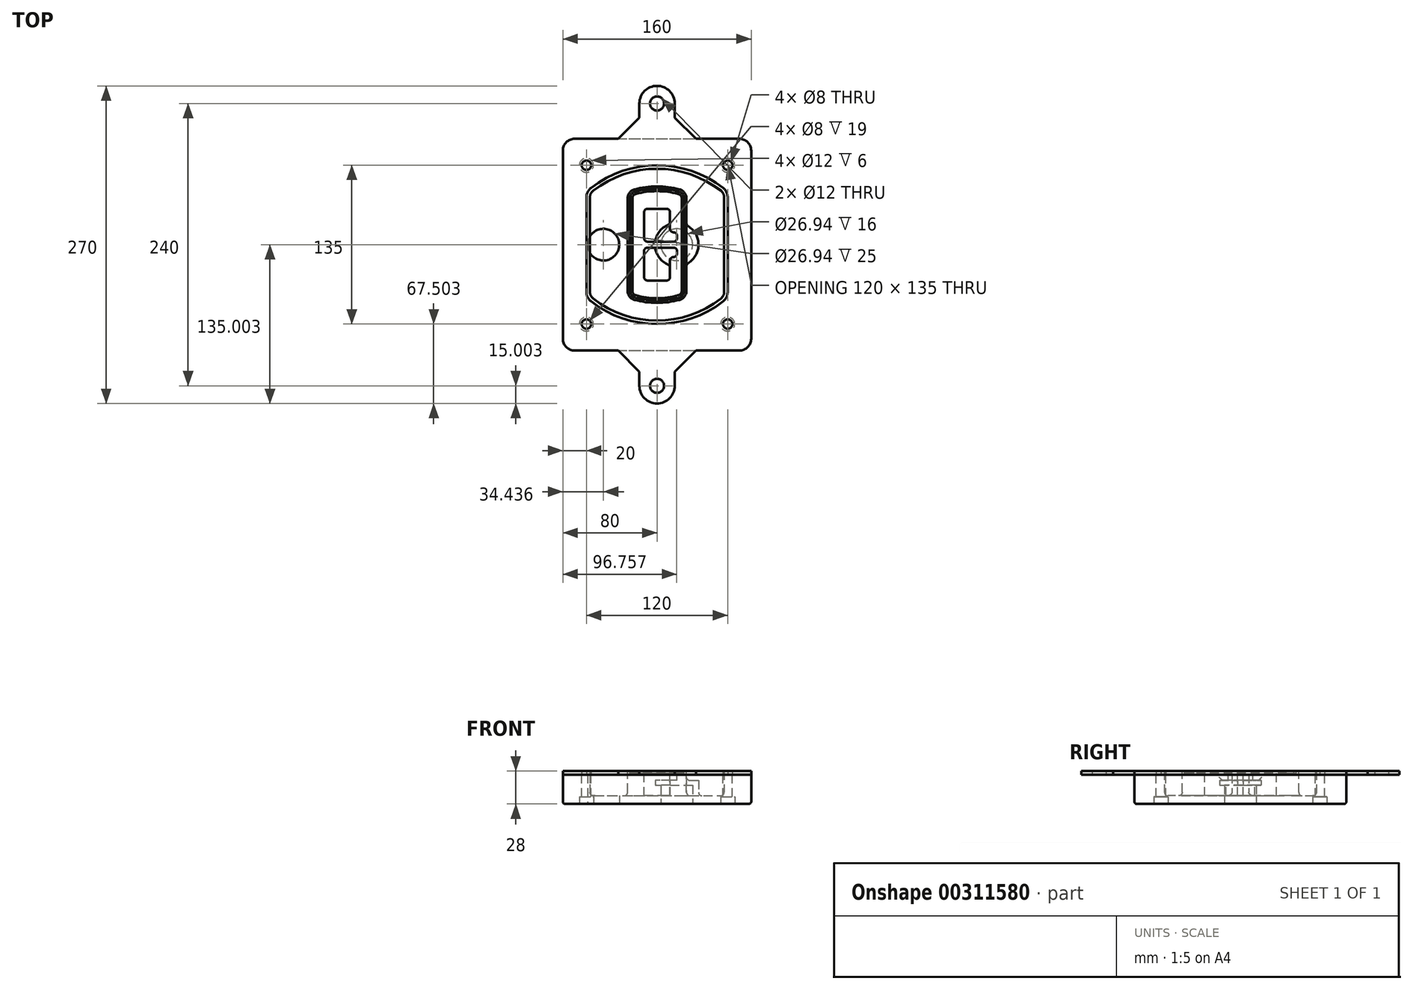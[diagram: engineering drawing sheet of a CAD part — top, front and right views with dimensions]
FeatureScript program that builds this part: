
annotation { "Feature Type Name" : "Feature", "Feature Type Description" : "" }
export const myFeature = defineFeature(function(context is Context, id is Id, definition is map)
    precondition{}
    {
        {
            var Q0;
            Q0=qCreatedBy(makeId("Top.planeOp"),FACE);
            var sketch = newSketch(context, id + "F0", { "sketchPlane" : qUnion([Q0])});
            skPoint(sketch, "E0.rect.middle", {"position": v(0, 0) * mm});
            skLineSegment(sketch, "E1.bottom", {"start": v(24.05, 28.38) * mm, "end": v(164.05, 28.38) * mm});
            skLineSegment(sketch, "E1.top", {"start": v(24.05, 208.38) * mm, "end": v(164.05, 208.38) * mm});
            skLineSegment(sketch, "E1.left", {"start": v(14.05, 38.38) * mm, "end": v(14.05, 198.38) * mm});
            skLineSegment(sketch, "E1.right", {"start": v(174.05, 38.38) * mm, "end": v(174.05, 198.38) * mm});
            skLineSegment(sketch, "E2", {"start": v(14.05, 208.38) * mm, "end": v(174.05, 28.38) * mm, "construction": true});
            skLineSegment(sketch, "E3", {"start": v(174.05, 208.38) * mm, "end": v(14.05, 28.38) * mm, "construction": true});
            skCircle(sketch, "E4", {"center": v(34.05, 185.88) * mm, "radius": 4 * mm});
            skCircle(sketch, "E5", {"center": v(154.05, 185.88) * mm, "radius": 4 * mm});
            skCircle(sketch, "E6", {"center": v(154.05, 50.88) * mm, "radius": 4 * mm});
            skCircle(sketch, "E7", {"center": v(34.05, 50.88) * mm, "radius": 4 * mm});
            skLineSegment(sketch, "E8", {"start": v(34.05, 185.88) * mm, "end": v(154.05, 185.88) * mm, "construction": true});
            skLineSegment(sketch, "E9", {"start": v(154.05, 185.88) * mm, "end": v(154.05, 50.88) * mm, "construction": true});
            skLineSegment(sketch, "E10", {"start": v(154.05, 50.88) * mm, "end": v(34.05, 50.88) * mm, "construction": true});
            skLineSegment(sketch, "E11", {"start": v(34.05, 50.88) * mm, "end": v(34.05, 185.88) * mm, "construction": true});
            skLineSegment(sketch, "E12", {"start": v(34.05, 158.68) * mm, "end": v(34.05, 78.09) * mm});
            skLineSegment(sketch, "E13", {"start": v(154.05, 158.68) * mm, "end": v(154.05, 78.09) * mm});
            skArc(sketch, "E14", {"start": v(150.2, 166.56) * mm, "mid": v(94.05, 185.88) * mm, "end": v(37.9, 166.56) * mm});
            skArc(sketch, "E15", {"start": v(37.9, 70.2) * mm, "mid": v(94.05, 50.88) * mm, "end": v(150.2, 70.2) * mm});
            skLineSegment(sketch, "E16", {"start": v(34.05, 118.38) * mm, "end": v(154.05, 118.38) * mm, "construction": true});
            skPoint(sketch, "E17.visualSharp", {"position": v(34.05, 73.38) * mm});
            skArc(sketch, "E17.filletArc", {"start": v(34.05, 78.09) * mm, "mid": v(35.06, 73.7) * mm, "end": v(37.9, 70.2) * mm});
            skPoint(sketch, "E18.visualSharp", {"position": v(34.05, 163.38) * mm});
            skArc(sketch, "E18.filletArc", {"start": v(37.9, 166.56) * mm, "mid": v(35.06, 163.06) * mm, "end": v(34.05, 158.68) * mm});
            skPoint(sketch, "E19.visualSharp", {"position": v(154.05, 163.38) * mm});
            skArc(sketch, "E19.filletArc", {"start": v(154.05, 158.68) * mm, "mid": v(153.04, 163.06) * mm, "end": v(150.2, 166.56) * mm});
            skPoint(sketch, "E20.visualSharp", {"position": v(154.05, 73.38) * mm});
            skArc(sketch, "E20.filletArc", {"start": v(150.2, 70.2) * mm, "mid": v(153.04, 73.7) * mm, "end": v(154.05, 78.09) * mm});
            skPoint(sketch, "E21.visualSharp", {"position": v(14.05, 208.38) * mm});
            skArc(sketch, "E21.filletArc", {"start": v(24.05, 208.38) * mm, "mid": v(16.98, 205.45) * mm, "end": v(14.05, 198.38) * mm});
            skPoint(sketch, "E22.visualSharp", {"position": v(174.05, 208.38) * mm});
            skArc(sketch, "E22.filletArc", {"start": v(174.05, 198.38) * mm, "mid": v(171.12, 205.45) * mm, "end": v(164.05, 208.38) * mm});
            skPoint(sketch, "E23.visualSharp", {"position": v(174.05, 28.38) * mm});
            skArc(sketch, "E23.filletArc", {"start": v(164.05, 28.38) * mm, "mid": v(171.12, 31.31) * mm, "end": v(174.05, 38.38) * mm});
            skPoint(sketch, "E24.visualSharp", {"position": v(14.05, 28.38) * mm});
            skArc(sketch, "E24.filletArc", {"start": v(14.05, 38.38) * mm, "mid": v(16.98, 31.31) * mm, "end": v(24.05, 28.38) * mm});
            skArc(sketch, "E25.0", {"start": v(151.05, 158.68) * mm, "mid": v(150.34, 161.75) * mm, "end": v(148.36, 164.2) * mm});
            skLineSegment(sketch, "E25.1", {"start": v(151.05, 158.68) * mm, "end": v(151.05, 78.09) * mm});
            skArc(sketch, "E25.2", {"start": v(148.36, 72.57) * mm, "mid": v(150.34, 75.02) * mm, "end": v(151.05, 78.09) * mm});
            skArc(sketch, "E25.3", {"start": v(39.74, 72.57) * mm, "mid": v(94.05, 53.88) * mm, "end": v(148.36, 72.57) * mm});
            skArc(sketch, "E25.4", {"start": v(37.05, 78.09) * mm, "mid": v(37.76, 75.02) * mm, "end": v(39.74, 72.57) * mm});
            skArc(sketch, "E25.5", {"start": v(148.36, 164.2) * mm, "mid": v(94.05, 182.88) * mm, "end": v(39.74, 164.2) * mm});
            skLineSegment(sketch, "E25.6", {"start": v(37.05, 158.68) * mm, "end": v(37.05, 78.09) * mm});
            skArc(sketch, "E25.7", {"start": v(39.74, 164.2) * mm, "mid": v(37.76, 161.75) * mm, "end": v(37.05, 158.68) * mm});
            skArc(sketch, "E26.0", {"start": v(35.43, 169.71) * mm, "mid": v(31.47, 164.82) * mm, "end": v(30.05, 158.68) * mm});
            skArc(sketch, "E26.1", {"start": v(152.67, 169.71) * mm, "mid": v(94.05, 189.88) * mm, "end": v(35.43, 169.71) * mm});
            skArc(sketch, "E26.2", {"start": v(158.05, 158.68) * mm, "mid": v(156.63, 164.82) * mm, "end": v(152.67, 169.71) * mm});
            skLineSegment(sketch, "E26.3", {"start": v(158.05, 158.68) * mm, "end": v(158.05, 78.09) * mm});
            skArc(sketch, "E26.4", {"start": v(152.67, 67.05) * mm, "mid": v(156.63, 71.95) * mm, "end": v(158.05, 78.09) * mm});
            skLineSegment(sketch, "E26.5", {"start": v(30.05, 158.68) * mm, "end": v(30.05, 78.09) * mm});
            skArc(sketch, "E26.6", {"start": v(35.43, 67.05) * mm, "mid": v(94.05, 46.88) * mm, "end": v(152.67, 67.05) * mm});
            skArc(sketch, "E26.7", {"start": v(30.05, 78.09) * mm, "mid": v(31.47, 71.95) * mm, "end": v(35.43, 67.05) * mm});
            skSolve(sketch);
        }
        {
            var Q0;
            Q0=makeQuery(id+"F0.imprint","IMPRINT",FACE,{"disambiguationData":[TD([[makeQuery(id+"F0.imprint","IMPRINT",EDGE,{"derivedFrom":sQuery(id+"F0.wireOp",EDGE,"E1.bottom")}),1.0]])]});
            var Q1;
            Q1=makeQuery(id+"F0.imprint","IMPRINT",FACE,{"disambiguationData":[TD([[makeQuery(id+"F0.imprint","IMPRINT",EDGE,{"derivedFrom":sQuery(id+"F0.wireOp",EDGE,"E12")}),1.0]])]});
            var Q2;
            Q2=makeQuery(id+"F0.imprint","IMPRINT",FACE,{"disambiguationData":[TD([[makeQuery(id+"F0.imprint","IMPRINT",EDGE,{"derivedFrom":sQuery(id+"F0.wireOp",EDGE,"E25.0")}),1.0]])]});
            var Q3;
            Q3=makeQuery(id+"F0.imprint","IMPRINT",FACE,{"disambiguationData":[TD([[makeQuery(id+"F0.imprint","IMPRINT",EDGE,{"derivedFrom":sQuery(id+"F0.wireOp",EDGE,"E12")}),-1.0]])]});
            extrude(context, id + "F1", {"entities" : qUnion([Q0, Q1, Q2, Q3]), "oppositeDirection" : true, "depth" : 25 * mm});
        }
        {
            var Q0;
            Q0=makeQuery(id+"F0.imprint","IMPRINT",FACE,{"disambiguationData":[TD([[makeQuery(id+"F0.imprint","IMPRINT",EDGE,{"derivedFrom":sQuery(id+"F0.wireOp",EDGE,"E12")}),1.0]])]});
            extrude(context, id + "F2", {"entities" : qUnion([Q0]), "operationType" : NewBodyOperationType.ADD, "depth" : 3 * mm});
        }
        {
            var Q0;
            Q0=makeQuery(id+"F0.imprint","IMPRINT",FACE,{"disambiguationData":[TD([[makeQuery(id+"F0.imprint","IMPRINT",EDGE,{"derivedFrom":sQuery(id+"F0.wireOp",EDGE,"E25.0")}),1.0]])]});
            extrude(context, id + "F3", {"entities" : qUnion([Q0]), "operationType" : NewBodyOperationType.REMOVE, "oppositeDirection" : true, "depth" : 18 * mm});
        }
        {
            var Q0;
            Q0=makeQuery(id+"F2.opExtrude","CAP_FACE",FACE,{"disambiguationData":[OSD([sQuery(id+"F0.wireOp",EDGE,"E12"),sQuery(id+"F0.wireOp",EDGE,"E13"),sQuery(id+"F0.wireOp",EDGE,"E14"),sQuery(id+"F0.wireOp",EDGE,"E15"),sQuery(id+"F0.wireOp",EDGE,"E17.filletArc"),sQuery(id+"F0.wireOp",EDGE,"E18.filletArc"),sQuery(id+"F0.wireOp",EDGE,"E19.filletArc"),sQuery(id+"F0.wireOp",EDGE,"E20.filletArc"),sQuery(id+"F0.wireOp",EDGE,"E25.0"),sQuery(id+"F0.wireOp",EDGE,"E25.1"),sQuery(id+"F0.wireOp",EDGE,"E25.2"),sQuery(id+"F0.wireOp",EDGE,"E25.3"),sQuery(id+"F0.wireOp",EDGE,"E25.4"),sQuery(id+"F0.wireOp",EDGE,"E25.5"),sQuery(id+"F0.wireOp",EDGE,"E25.6"),sQuery(id+"F0.wireOp",EDGE,"E25.7")])],"isStart":false});
            var sketch = newSketch(context, id + "F4", { "sketchPlane" : qUnion([Q0])});
            skArc(sketch, "E27.0", {"start": v(74.97, 71.41) * mm, "mid": v(94.05, 68.88) * mm, "end": v(113.13, 71.41) * mm});
            skArc(sketch, "E28.0", {"start": v(113.13, 165.35) * mm, "mid": v(94.05, 167.88) * mm, "end": v(74.97, 165.35) * mm});
            skLineSegment(sketch, "E29", {"start": v(69.05, 157.63) * mm, "end": v(69.05, 79.14) * mm});
            skLineSegment(sketch, "E30", {"start": v(119.05, 157.63) * mm, "end": v(119.05, 79.14) * mm});
            skLineSegment(sketch, "E31", {"start": v(69.05, 163.48) * mm, "end": v(119.05, 163.48) * mm, "construction": true});
            skLineSegment(sketch, "E32", {"start": v(69.05, 73.28) * mm, "end": v(119.05, 73.28) * mm, "construction": true});
            skPoint(sketch, "E33.visualSharp", {"position": v(69.05, 163.48) * mm});
            skArc(sketch, "E33.filletArc", {"start": v(74.97, 165.35) * mm, "mid": v(70.7, 162.5) * mm, "end": v(69.05, 157.63) * mm});
            skPoint(sketch, "E34.visualSharp", {"position": v(119.05, 163.48) * mm});
            skArc(sketch, "E34.filletArc", {"start": v(119.05, 157.63) * mm, "mid": v(117.4, 162.5) * mm, "end": v(113.13, 165.35) * mm});
            skPoint(sketch, "E35.visualSharp", {"position": v(119.05, 73.28) * mm});
            skArc(sketch, "E35.filletArc", {"start": v(113.13, 71.41) * mm, "mid": v(117.4, 74.27) * mm, "end": v(119.05, 79.14) * mm});
            skPoint(sketch, "E36.visualSharp", {"position": v(69.05, 73.28) * mm});
            skArc(sketch, "E36.filletArc", {"start": v(69.05, 79.14) * mm, "mid": v(70.7, 74.27) * mm, "end": v(74.97, 71.41) * mm});
            skArc(sketch, "E37.0", {"start": v(148.36, 164.2) * mm, "mid": v(94.05, 182.88) * mm, "end": v(39.74, 164.2) * mm});
            skArc(sketch, "E37.1", {"start": v(39.74, 164.2) * mm, "mid": v(37.76, 161.75) * mm, "end": v(37.05, 158.68) * mm});
            skLineSegment(sketch, "E37.2", {"start": v(37.05, 158.68) * mm, "end": v(37.05, 78.09) * mm});
            skArc(sketch, "E37.3", {"start": v(37.05, 78.09) * mm, "mid": v(37.76, 75.02) * mm, "end": v(39.74, 72.57) * mm});
            skArc(sketch, "E37.4", {"start": v(39.74, 72.57) * mm, "mid": v(94.05, 53.88) * mm, "end": v(148.36, 72.57) * mm});
            skArc(sketch, "E37.5", {"start": v(148.36, 72.57) * mm, "mid": v(150.34, 75.02) * mm, "end": v(151.05, 78.09) * mm});
            skLineSegment(sketch, "E37.6", {"start": v(151.05, 158.68) * mm, "end": v(151.05, 78.09) * mm});
            skArc(sketch, "E37.7", {"start": v(151.05, 158.68) * mm, "mid": v(150.34, 161.75) * mm, "end": v(148.36, 164.2) * mm});
            skLineSegment(sketch, "E38.0", {"start": v(117.05, 157.63) * mm, "end": v(117.05, 79.14) * mm});
            skArc(sketch, "E38.1", {"start": v(112.61, 73.34) * mm, "mid": v(115.81, 75.49) * mm, "end": v(117.05, 79.14) * mm});
            skArc(sketch, "E38.2", {"start": v(75.49, 73.34) * mm, "mid": v(94.05, 70.88) * mm, "end": v(112.61, 73.34) * mm});
            skArc(sketch, "E38.3", {"start": v(71.05, 79.14) * mm, "mid": v(72.29, 75.49) * mm, "end": v(75.49, 73.34) * mm});
            skLineSegment(sketch, "E38.4", {"start": v(71.05, 157.63) * mm, "end": v(71.05, 79.14) * mm});
            skArc(sketch, "E38.5", {"start": v(117.05, 157.63) * mm, "mid": v(115.81, 161.28) * mm, "end": v(112.61, 163.42) * mm});
            skArc(sketch, "E38.6", {"start": v(75.49, 163.42) * mm, "mid": v(72.29, 161.28) * mm, "end": v(71.05, 157.63) * mm});
            skArc(sketch, "E38.7", {"start": v(112.61, 163.42) * mm, "mid": v(94.05, 165.88) * mm, "end": v(75.49, 163.42) * mm});
            skArc(sketch, "E39.0", {"start": v(115.05, 157.63) * mm, "mid": v(114.23, 160.06) * mm, "end": v(112.1, 161.5) * mm});
            skLineSegment(sketch, "E39.1", {"start": v(115.05, 157.63) * mm, "end": v(115.05, 79.14) * mm});
            skArc(sketch, "E39.2", {"start": v(112.1, 75.27) * mm, "mid": v(114.23, 76.7) * mm, "end": v(115.05, 79.14) * mm});
            skArc(sketch, "E39.3", {"start": v(76, 75.27) * mm, "mid": v(94.05, 72.88) * mm, "end": v(112.1, 75.27) * mm});
            skArc(sketch, "E39.4", {"start": v(73.05, 79.14) * mm, "mid": v(73.87, 76.7) * mm, "end": v(76, 75.27) * mm});
            skArc(sketch, "E39.5", {"start": v(112.1, 161.5) * mm, "mid": v(94.05, 163.88) * mm, "end": v(76, 161.5) * mm});
            skLineSegment(sketch, "E39.6", {"start": v(73.05, 157.63) * mm, "end": v(73.05, 79.14) * mm});
            skArc(sketch, "E39.7", {"start": v(76, 161.5) * mm, "mid": v(73.87, 160.06) * mm, "end": v(73.05, 157.63) * mm});
            skLineSegment(sketch, "E40", {"start": v(69.05, 118.38) * mm, "end": v(119.05, 118.38) * mm, "construction": true});
            skLineSegment(sketch, "E41", {"start": v(83.05, 123.88) * mm, "end": v(83.05, 145.88) * mm});
            skLineSegment(sketch, "E42", {"start": v(86.05, 148.88) * mm, "end": v(102.05, 148.88) * mm});
            skLineSegment(sketch, "E43", {"start": v(105.05, 145.88) * mm, "end": v(105.05, 131.88) * mm});
            skLineSegment(sketch, "E44", {"start": v(108.05, 128.88) * mm, "end": v(108.05, 128.88) * mm});
            skLineSegment(sketch, "E45", {"start": v(111.05, 125.88) * mm, "end": v(111.05, 123.88) * mm});
            skLineSegment(sketch, "E46", {"start": v(108.05, 120.88) * mm, "end": v(86.05, 120.88) * mm});
            skPoint(sketch, "E47.visualSharp", {"position": v(83.05, 148.88) * mm});
            skArc(sketch, "E47.filletArc", {"start": v(86.05, 148.88) * mm, "mid": v(83.93, 148) * mm, "end": v(83.05, 145.88) * mm});
            skPoint(sketch, "E48.visualSharp", {"position": v(105.05, 148.88) * mm});
            skArc(sketch, "E48.filletArc", {"start": v(105.05, 145.88) * mm, "mid": v(104.17, 148) * mm, "end": v(102.05, 148.88) * mm});
            skPoint(sketch, "E49.visualSharp", {"position": v(105.05, 128.88) * mm});
            skArc(sketch, "E49.filletArc", {"start": v(105.05, 131.88) * mm, "mid": v(105.93, 129.76) * mm, "end": v(108.05, 128.88) * mm});
            skPoint(sketch, "E50.visualSharp", {"position": v(111.05, 128.88) * mm});
            skArc(sketch, "E50.filletArc", {"start": v(111.05, 125.88) * mm, "mid": v(110.17, 128) * mm, "end": v(108.05, 128.88) * mm});
            skPoint(sketch, "E51.visualSharp", {"position": v(111.05, 120.88) * mm});
            skArc(sketch, "E51.filletArc", {"start": v(108.05, 120.88) * mm, "mid": v(110.17, 121.76) * mm, "end": v(111.05, 123.88) * mm});
            skPoint(sketch, "E52.visualSharp", {"position": v(83.05, 120.88) * mm});
            skArc(sketch, "E52.filletArc", {"start": v(83.05, 123.88) * mm, "mid": v(83.93, 121.76) * mm, "end": v(86.05, 120.88) * mm});
            skLineSegment(sketch, "E53.0.MirrorCS", {"start": v(108.05, 115.88) * mm, "end": v(86.05, 115.88) * mm});
            skArc(sketch, "E54.0.MirrorCS", {"start": v(83.05, 112.88) * mm, "mid": v(83.93, 115) * mm, "end": v(86.05, 115.88) * mm});
            skLineSegment(sketch, "E55.0.MirrorCS", {"start": v(83.05, 112.88) * mm, "end": v(83.05, 90.88) * mm});
            skArc(sketch, "E56.0.MirrorCS", {"start": v(86.05, 87.88) * mm, "mid": v(83.93, 88.76) * mm, "end": v(83.05, 90.88) * mm});
            skLineSegment(sketch, "E57.0.MirrorCS", {"start": v(86.05, 87.88) * mm, "end": v(102.05, 87.88) * mm});
            skArc(sketch, "E58.0.MirrorCS", {"start": v(105.05, 90.88) * mm, "mid": v(104.17, 88.76) * mm, "end": v(102.05, 87.88) * mm});
            skLineSegment(sketch, "E59.0.MirrorCS", {"start": v(105.05, 90.88) * mm, "end": v(105.05, 104.88) * mm});
            skArc(sketch, "E60.0.MirrorCS", {"start": v(105.05, 104.88) * mm, "mid": v(105.93, 107) * mm, "end": v(108.05, 107.88) * mm});
            skArc(sketch, "E61.0.MirrorCS", {"start": v(111.05, 110.88) * mm, "mid": v(110.17, 108.76) * mm, "end": v(108.05, 107.88) * mm});
            skLineSegment(sketch, "E62.0.MirrorCS", {"start": v(111.05, 110.88) * mm, "end": v(111.05, 112.88) * mm});
            skArc(sketch, "E63.0.MirrorCS", {"start": v(108.05, 115.88) * mm, "mid": v(110.17, 115) * mm, "end": v(111.05, 112.88) * mm});
            skSolve(sketch);
        }
        {
            var Q0;
            Q0=makeQuery(id+"F4.imprint","IMPRINT",FACE,{"disambiguationData":[TD([[makeQuery(id+"F4.imprint","IMPRINT",EDGE,{"derivedFrom":sQuery(id+"F4.wireOp",EDGE,"E27.0")}),1.0]])]});
            var Q1;
            Q1=makeQuery(id+"F4.imprint","IMPRINT",FACE,{"disambiguationData":[TD([[makeQuery(id+"F4.imprint","IMPRINT",EDGE,{"derivedFrom":sQuery(id+"F4.wireOp",EDGE,"E38.0")}),-1.0]])]});
            var Q2;
            Q2=makeQuery(id+"F4.imprint","IMPRINT",FACE,{"disambiguationData":[TD([[makeQuery(id+"F4.imprint","IMPRINT",EDGE,{"derivedFrom":sQuery(id+"F4.wireOp",EDGE,"E39.0")}),1.0]])]});
            extrude(context, id + "F5", {"entities" : qUnion([Q0, Q1, Q2]), "operationType" : NewBodyOperationType.ADD, "endBound" : BoundingType.UP_TO_NEXT, "oppositeDirection" : true, "depth" : 25 * mm});
        }
        {
            var Q0;
            Q0=makeQuery(id+"F4.imprint","IMPRINT",FACE,{"disambiguationData":[TD([[makeQuery(id+"F4.imprint","IMPRINT",EDGE,{"derivedFrom":sQuery(id+"F4.wireOp",EDGE,"E38.0")}),-1.0]])]});
            extrude(context, id + "F6", {"entities" : qUnion([Q0]), "operationType" : NewBodyOperationType.REMOVE, "oppositeDirection" : true, "depth" : 2 * mm});
        }
        {
            var Q0;
            Q0=makeQuery(id+"F1.opExtrude","CAP_FACE",FACE,{"disambiguationData":[OSD([sQuery(id+"F0.wireOp",EDGE,"E1.bottom"),sQuery(id+"F0.wireOp",EDGE,"E1.top"),sQuery(id+"F0.wireOp",EDGE,"E1.left"),sQuery(id+"F0.wireOp",EDGE,"E1.right"),sQuery(id+"F0.wireOp",EDGE,"E4"),sQuery(id+"F0.wireOp",EDGE,"E5"),sQuery(id+"F0.wireOp",EDGE,"E6"),sQuery(id+"F0.wireOp",EDGE,"E7"),sQuery(id+"F0.wireOp",EDGE,"E21.filletArc"),sQuery(id+"F0.wireOp",EDGE,"E22.filletArc"),sQuery(id+"F0.wireOp",EDGE,"E23.filletArc"),sQuery(id+"F0.wireOp",EDGE,"E24.filletArc")])],"isStart":false});
            var sketch = newSketch(context, id + "F7", { "sketchPlane" : qUnion([Q0])});
            skCircle(sketch, "E64", {"center": v(110.8, -118.38) * mm, "radius": 13.47 * mm});
            skCircle(sketch, "E65", {"center": v(48.49, -118.38) * mm, "radius": 13.47 * mm});
            skLineSegment(sketch, "E66", {"start": v(174.05, -118.38) * mm, "end": v(14.05, -118.38) * mm});
            skCircle(sketch, "E67", {"center": v(110.8, -118.38) * mm, "radius": 18.47 * mm});
            skCircle(sketch, "E68", {"center": v(154.05, -185.88) * mm, "radius": 6 * mm});
            skCircle(sketch, "E69", {"center": v(34.05, -185.88) * mm, "radius": 6 * mm});
            skCircle(sketch, "E70", {"center": v(34.05, -50.88) * mm, "radius": 6 * mm});
            skCircle(sketch, "E71", {"center": v(154.05, -50.88) * mm, "radius": 6 * mm});
            skSolve(sketch);
        }
        {
            var Q0;
            {var subQ1=sQuery(id+"F7.wireOp",EDGE,"E66");var subQ4=sQuery(id+"F7.wireOp",EDGE,"E64");var subQ6=makeQuery(id+"F7.imprint","INTERSECT",VERTEX,{"disambiguationData":[OD(0.0)],"derivedFrom":[subQ4,subQ1]});Q0=makeQuery(id+"F7.imprint","IMPRINT",FACE,{"disambiguationData":[TD([[makeQuery(id+"F7.imprint","IMPRINT",EDGE,{"disambiguationData":[TD([[subQ6,-1.0]])],"derivedFrom":subQ4}),-1.0]])]});}
            var Q1;
            {var subQ0=sQuery(id+"F7.wireOp",EDGE,"E66");var subQ1=sQuery(id+"F7.wireOp",EDGE,"E64");var subQ3=makeQuery(id+"F7.imprint","INTERSECT",VERTEX,{"disambiguationData":[OD(0.0)],"derivedFrom":[subQ1,subQ0]});Q1=makeQuery(id+"F7.imprint","IMPRINT",FACE,{"disambiguationData":[TD([[makeQuery(id+"F7.imprint","IMPRINT",EDGE,{"disambiguationData":[TD([[subQ3,-1.0]])],"derivedFrom":subQ1}),1.0]])]});}
            var Q2;
            {var subQ0=sQuery(id+"F7.wireOp",EDGE,"E66");var subQ1=sQuery(id+"F7.wireOp",EDGE,"E64");var subQ3=makeQuery(id+"F7.imprint","INTERSECT",VERTEX,{"disambiguationData":[OD(0.0)],"derivedFrom":[subQ1,subQ0]});Q2=makeQuery(id+"F7.imprint","IMPRINT",FACE,{"disambiguationData":[TD([[makeQuery(id+"F7.imprint","IMPRINT",EDGE,{"disambiguationData":[TD([[subQ3,1.0]])],"derivedFrom":subQ1}),1.0]])]});}
            var Q3;
            {var subQ1=sQuery(id+"F7.wireOp",EDGE,"E66");var subQ4=sQuery(id+"F7.wireOp",EDGE,"E64");var subQ6=makeQuery(id+"F7.imprint","INTERSECT",VERTEX,{"disambiguationData":[OD(0.0)],"derivedFrom":[subQ4,subQ1]});Q3=makeQuery(id+"F7.imprint","IMPRINT",FACE,{"disambiguationData":[TD([[makeQuery(id+"F7.imprint","IMPRINT",EDGE,{"disambiguationData":[TD([[subQ6,1.0]])],"derivedFrom":subQ4}),-1.0]])]});}
            extrude(context, id + "F8", {"entities" : qUnion([Q0, Q1, Q2, Q3]), "operationType" : NewBodyOperationType.ADD, "oppositeDirection" : true, "depth" : 20 * mm});
        }
        {
            var Q0;
            {var subQ0=sQuery(id+"F7.wireOp",EDGE,"E66");var subQ1=sQuery(id+"F7.wireOp",EDGE,"E64");var subQ3=makeQuery(id+"F7.imprint","INTERSECT",VERTEX,{"disambiguationData":[OD(0.0)],"derivedFrom":[subQ1,subQ0]});Q0=makeQuery(id+"F7.imprint","IMPRINT",FACE,{"disambiguationData":[TD([[makeQuery(id+"F7.imprint","IMPRINT",EDGE,{"disambiguationData":[TD([[subQ3,-1.0]])],"derivedFrom":subQ1}),1.0]])]});}
            var Q1;
            {var subQ0=sQuery(id+"F7.wireOp",EDGE,"E66");var subQ1=sQuery(id+"F7.wireOp",EDGE,"E64");var subQ3=makeQuery(id+"F7.imprint","INTERSECT",VERTEX,{"disambiguationData":[OD(0.0)],"derivedFrom":[subQ1,subQ0]});Q1=makeQuery(id+"F7.imprint","IMPRINT",FACE,{"disambiguationData":[TD([[makeQuery(id+"F7.imprint","IMPRINT",EDGE,{"disambiguationData":[TD([[subQ3,1.0]])],"derivedFrom":subQ1}),1.0]])]});}
            extrude(context, id + "F9", {"entities" : qUnion([Q0, Q1]), "operationType" : NewBodyOperationType.REMOVE, "oppositeDirection" : true, "depth" : 16 * mm});
        }
        {
            var Q0;
            {var subQ0=sQuery(id+"F7.wireOp",EDGE,"E66");var subQ1=sQuery(id+"F7.wireOp",EDGE,"E65");var subQ3=makeQuery(id+"F7.imprint","INTERSECT",VERTEX,{"disambiguationData":[OD(0.0)],"derivedFrom":[subQ1,subQ0]});Q0=makeQuery(id+"F7.imprint","IMPRINT",FACE,{"disambiguationData":[TD([[makeQuery(id+"F7.imprint","IMPRINT",EDGE,{"disambiguationData":[TD([[subQ3,-1.0]])],"derivedFrom":subQ1}),1.0]])]});}
            var Q1;
            {var subQ0=sQuery(id+"F7.wireOp",EDGE,"E66");var subQ1=sQuery(id+"F7.wireOp",EDGE,"E65");var subQ3=makeQuery(id+"F7.imprint","INTERSECT",VERTEX,{"disambiguationData":[OD(0.0)],"derivedFrom":[subQ1,subQ0]});Q1=makeQuery(id+"F7.imprint","IMPRINT",FACE,{"disambiguationData":[TD([[makeQuery(id+"F7.imprint","IMPRINT",EDGE,{"disambiguationData":[TD([[subQ3,1.0]])],"derivedFrom":subQ1}),1.0]])]});}
            extrude(context, id + "F10", {"entities" : qUnion([Q0, Q1]), "operationType" : NewBodyOperationType.REMOVE, "oppositeDirection" : true, "depth" : 25 * mm});
        }
        {
            var Q0;
            Q0=makeQuery(id+"F7.imprint","IMPRINT",FACE,{"disambiguationData":[TD([[makeQuery(id+"F7.imprint","IMPRINT",EDGE,{"derivedFrom":sQuery(id+"F7.wireOp",EDGE,"E68")}),1.0]])]});
            var Q1;
            Q1=makeQuery(id+"F7.imprint","IMPRINT",FACE,{"disambiguationData":[TD([[makeQuery(id+"F7.imprint","IMPRINT",EDGE,{"derivedFrom":makeQuery(id+"F1.opExtrude","CAP_EDGE",EDGE,{"disambiguationData":[OSD([sQuery(id+"F0.wireOp",EDGE,"E5")])],"isStart":false})}),-1.0]])]});
            var Q2;
            Q2=makeQuery(id+"F7.imprint","IMPRINT",FACE,{"disambiguationData":[TD([[makeQuery(id+"F7.imprint","IMPRINT",EDGE,{"derivedFrom":sQuery(id+"F7.wireOp",EDGE,"E69")}),1.0]])]});
            var Q3;
            Q3=makeQuery(id+"F7.imprint","IMPRINT",FACE,{"disambiguationData":[TD([[makeQuery(id+"F7.imprint","IMPRINT",EDGE,{"derivedFrom":makeQuery(id+"F1.opExtrude","CAP_EDGE",EDGE,{"disambiguationData":[OSD([sQuery(id+"F0.wireOp",EDGE,"E4")])],"isStart":false})}),-1.0]])]});
            var Q4;
            Q4=makeQuery(id+"F7.imprint","IMPRINT",FACE,{"disambiguationData":[TD([[makeQuery(id+"F7.imprint","IMPRINT",EDGE,{"derivedFrom":sQuery(id+"F7.wireOp",EDGE,"E70")}),1.0]])]});
            var Q5;
            Q5=makeQuery(id+"F7.imprint","IMPRINT",FACE,{"disambiguationData":[TD([[makeQuery(id+"F7.imprint","IMPRINT",EDGE,{"derivedFrom":makeQuery(id+"F1.opExtrude","CAP_EDGE",EDGE,{"disambiguationData":[OSD([sQuery(id+"F0.wireOp",EDGE,"E7")])],"isStart":false})}),-1.0]])]});
            var Q6;
            Q6=makeQuery(id+"F7.imprint","IMPRINT",FACE,{"disambiguationData":[TD([[makeQuery(id+"F7.imprint","IMPRINT",EDGE,{"derivedFrom":sQuery(id+"F7.wireOp",EDGE,"E71")}),1.0]])]});
            var Q7;
            Q7=makeQuery(id+"F7.imprint","IMPRINT",FACE,{"disambiguationData":[TD([[makeQuery(id+"F7.imprint","IMPRINT",EDGE,{"derivedFrom":makeQuery(id+"F1.opExtrude","CAP_EDGE",EDGE,{"disambiguationData":[OSD([sQuery(id+"F0.wireOp",EDGE,"E6")])],"isStart":false})}),-1.0]])]});
            extrude(context, id + "F11", {"entities" : qUnion([Q0, Q1, Q2, Q3, Q4, Q5, Q6, Q7]), "operationType" : NewBodyOperationType.REMOVE, "oppositeDirection" : true, "depth" : 6 * mm});
        }
        {
            var Q0;
            Q0=makeQuery(id+"F9.boolean.opBoolean","COPY",FACE,{"derivedFrom":makeQuery(id+"F9.opExtrude","CAP_FACE",FACE,{"disambiguationData":[OSD([sQuery(id+"F7.wireOp",EDGE,"E64")])],"isStart":false})});
            var sketch = newSketch(context, id + "F12", { "sketchPlane" : qUnion([Q0])});
            skArc(sketch, "E72.0", {"start": v(105.05, -100.83) * mm, "mid": v(96.62, -106.56) * mm, "end": v(92.5, -115.88) * mm});
            skArc(sketch, "E72.1", {"start": v(92.5, -120.88) * mm, "mid": v(96.62, -130.2) * mm, "end": v(105.05, -135.93) * mm});
            skLineSegment(sketch, "E73", {"start": v(92.5, -120.88) * mm, "end": v(108.05, -120.88) * mm});
            skLineSegment(sketch, "E74.0", {"start": v(108.05, -115.88) * mm, "end": v(92.5, -115.88) * mm});
            skArc(sketch, "E74.1", {"start": v(108.05, -115.88) * mm, "mid": v(110.17, -115) * mm, "end": v(111.05, -112.88) * mm});
            skLineSegment(sketch, "E74.2", {"start": v(111.05, -110.88) * mm, "end": v(111.05, -112.88) * mm});
            skArc(sketch, "E74.3", {"start": v(111.05, -110.88) * mm, "mid": v(110.17, -108.76) * mm, "end": v(108.05, -107.88) * mm});
            skArc(sketch, "E74.4", {"start": v(105.05, -104.88) * mm, "mid": v(105.93, -107) * mm, "end": v(108.05, -107.88) * mm});
            skLineSegment(sketch, "E74.5", {"start": v(105.05, -100.83) * mm, "end": v(105.05, -104.88) * mm});
            skLineSegment(sketch, "E74.7", {"start": v(108.05, -120.88) * mm, "end": v(92.5, -120.88) * mm});
            skArc(sketch, "E74.8", {"start": v(108.05, -120.88) * mm, "mid": v(110.17, -121.76) * mm, "end": v(111.05, -123.88) * mm});
            skLineSegment(sketch, "E74.9", {"start": v(111.05, -125.88) * mm, "end": v(111.05, -123.88) * mm});
            skArc(sketch, "E74.10", {"start": v(111.05, -125.88) * mm, "mid": v(110.17, -128) * mm, "end": v(108.05, -128.88) * mm});
            skArc(sketch, "E74.11", {"start": v(105.05, -131.88) * mm, "mid": v(105.93, -129.76) * mm, "end": v(108.05, -128.88) * mm});
            skLineSegment(sketch, "E74.12", {"start": v(105.05, -135.93) * mm, "end": v(105.05, -131.88) * mm});
            skPoint(sketch, "E75.orphan", {"position": v(105.05, -145.88) * mm});
            skPoint(sketch, "E76.orphan", {"position": v(86.05, -120.88) * mm});
            skPoint(sketch, "E77.orphan", {"position": v(86.05, -115.88) * mm});
            skPoint(sketch, "E78.orphan", {"position": v(105.05, -90.88) * mm});
            skSolve(sketch);
        }
        {
            var Q0;
            {var subQ7=sQuery(id+"F12.wireOp",EDGE,"E72.0");var subQ14=sQuery(id+"F12.wireOp",EDGE,"E72.1");var subQ16=sQuery(id+"F12.wireOp",EDGE,"E74.1");var subQ18=sQuery(id+"F12.wireOp",EDGE,"E74.8");Q0=qUnion([makeQuery(id+"F12.imprint","IMPRINT",FACE,{"disambiguationData":[TD([[makeQuery(id+"F12.imprint","IMPRINT",EDGE,{"derivedFrom":subQ7}),1.0]])]}),makeQuery(id+"F12.imprint","IMPRINT",FACE,{"disambiguationData":[TD([[makeQuery(id+"F12.imprint","IMPRINT",EDGE,{"derivedFrom":subQ14}),1.0]])]}),makeQuery(id+"F12.imprint","IMPRINT",FACE,{"disambiguationData":[TD([[makeQuery(id+"F12.imprint","IMPRINT",EDGE,{"derivedFrom":subQ16}),1.0]])]}),makeQuery(id+"F12.imprint","IMPRINT",FACE,{"disambiguationData":[TD([[makeQuery(id+"F12.imprint","IMPRINT",EDGE,{"derivedFrom":subQ18}),-1.0]])]})]);}
            var Q1;
            Q1=makeQuery(id+"F5.boolean.opBoolean","SPLIT",FACE,{"disambiguationData":[TD([makeQuery(id+"F5.opExtrude","SWEPT_FACE",FACE,{"disambiguationData":[OSD([sQuery(id+"F4.wireOp",EDGE,"E41")])]})])],"derivedFrom":makeQuery(id+"F3.boolean.opBoolean","COPY",FACE,{"derivedFrom":makeQuery(id+"F3.opExtrude","CAP_FACE",FACE,{"disambiguationData":[OSD([sQuery(id+"F0.wireOp",EDGE,"E25.0"),sQuery(id+"F0.wireOp",EDGE,"E25.1"),sQuery(id+"F0.wireOp",EDGE,"E25.2"),sQuery(id+"F0.wireOp",EDGE,"E25.3"),sQuery(id+"F0.wireOp",EDGE,"E25.4"),sQuery(id+"F0.wireOp",EDGE,"E25.5"),sQuery(id+"F0.wireOp",EDGE,"E25.6"),sQuery(id+"F0.wireOp",EDGE,"E25.7")])],"isStart":false})})});
            extrude(context, id + "F13", {"entities" : qUnion([Q0]), "operationType" : NewBodyOperationType.REMOVE, "endBound" : BoundingType.UP_TO_SURFACE, "endBoundEntityFace" : qUnion([Q1]), "depth" : 25 * mm});
        }
        {
            var Q0;
            Q0=makeQuery(id+"F3.boolean.opBoolean","COPY",EDGE,{"derivedFrom":makeQuery(id+"F3.opExtrude","CAP_EDGE",EDGE,{"disambiguationData":[OSD([sQuery(id+"F0.wireOp",EDGE,"E25.6")])],"isStart":false})});
            var Q1;
            Q1=makeQuery(id+"F8.boolean.opBoolean","INTERSECT",EDGE,{"derivedFrom":[makeQuery(id+"F5.opExtrude","SWEPT_FACE",FACE,{"disambiguationData":[OSD([sQuery(id+"F4.wireOp",EDGE,"E30")])]}),makeQuery(id+"F8.opExtrude","CAP_FACE",FACE,{"disambiguationData":[OSD([sQuery(id+"F7.wireOp",EDGE,"E67")])],"isStart":false})]});
            var Q2;
            Q2=makeQuery(id+"F8.boolean.opBoolean","INTERSECT",EDGE,{"disambiguationData":[OD(1.0)],"derivedFrom":[makeQuery(id+"F5.opExtrude","SWEPT_FACE",FACE,{"disambiguationData":[OSD([sQuery(id+"F4.wireOp",EDGE,"E30")])]}),makeQuery(id+"F8.opExtrude","SWEPT_FACE",FACE,{"disambiguationData":[OSD([sQuery(id+"F7.wireOp",EDGE,"E67")])]})]});
            var Q3;
            {var subQ0=sQuery(id+"F4.wireOp",EDGE,"E30");Q3=makeQuery(id+"F8.boolean.opBoolean","SPLIT",EDGE,{"disambiguationData":[TD([makeQuery(id+"F5.opExtrude","SWEPT_FACE",FACE,{"disambiguationData":[OSD([sQuery(id+"F4.wireOp",EDGE,"E35.filletArc")])]})])],"derivedFrom":makeQuery(id+"F5.opExtrude","CAP_EDGE",EDGE,{"disambiguationData":[OSD([subQ0])],"isStart":false})});}
            var Q4;
            {var subQ0=sQuery(id+"F0.wireOp",EDGE,"E25.7");var subQ1=sQuery(id+"F0.wireOp",EDGE,"E25.1");var subQ2=sQuery(id+"F0.wireOp",EDGE,"E25.6");var subQ3=sQuery(id+"F0.wireOp",EDGE,"E25.5");var subQ4=sQuery(id+"F0.wireOp",EDGE,"E25.4");var subQ5=sQuery(id+"F0.wireOp",EDGE,"E25.0");var subQ6=sQuery(id+"F0.wireOp",EDGE,"E25.2");var subQ7=sQuery(id+"F0.wireOp",EDGE,"E25.3");Q4=makeQuery(id+"F8.boolean.opBoolean","INTERSECT",EDGE,{"derivedFrom":[makeQuery(id+"F5.boolean.opBoolean","SPLIT",FACE,{"disambiguationData":[TD([makeQuery(id+"F2.opExtrude","SWEPT_FACE",FACE,{"disambiguationData":[OSD([subQ5])]})])],"derivedFrom":makeQuery(id+"F3.boolean.opBoolean","COPY",FACE,{"derivedFrom":makeQuery(id+"F3.opExtrude","CAP_FACE",FACE,{"disambiguationData":[OSD([subQ5,subQ1,subQ6,subQ7,subQ4,subQ3,subQ2,subQ0])],"isStart":false})})}),makeQuery(id+"F8.opExtrude","SWEPT_FACE",FACE,{"disambiguationData":[OSD([sQuery(id+"F7.wireOp",EDGE,"E67")])]})]});}
            var Q5;
            Q5=makeQuery(id+"F8.boolean.opBoolean","INTERSECT",EDGE,{"disambiguationData":[OD(0.0)],"derivedFrom":[makeQuery(id+"F5.opExtrude","SWEPT_FACE",FACE,{"disambiguationData":[OSD([sQuery(id+"F4.wireOp",EDGE,"E30")])]}),makeQuery(id+"F8.opExtrude","SWEPT_FACE",FACE,{"disambiguationData":[OSD([sQuery(id+"F7.wireOp",EDGE,"E67")])]})]});
            fillet(context, id + "F14", {"entities" : qUnion([Q0, Q1, Q2, Q3, Q4, Q5]), "radius" : 3 * mm, "tangentPropagation" : true, "allowEdgeOverflow" : false});
        }
        {
            var Q0;
            Q0=makeQuery(id+"F1.opExtrude","CAP_EDGE",EDGE,{"disambiguationData":[OSD([sQuery(id+"F0.wireOp",EDGE,"E1.bottom")])],"isStart":false});
            fillet(context, id + "F15", {"entities" : qUnion([Q0]), "radius" : 2 * mm, "tangentPropagation" : true, "allowEdgeOverflow" : false});
        }
        {
            var Q0;
            {var subQ0=sQuery(id+"F0.wireOp",EDGE,"E22.filletArc");var subQ1=sQuery(id+"F0.wireOp",EDGE,"E7");var subQ2=sQuery(id+"F0.wireOp",EDGE,"E6");var subQ3=sQuery(id+"F0.wireOp",EDGE,"E5");var subQ4=sQuery(id+"F0.wireOp",EDGE,"E4");var subQ5=sQuery(id+"F0.wireOp",EDGE,"E1.bottom");var subQ6=sQuery(id+"F0.wireOp",EDGE,"E21.filletArc");var subQ7=sQuery(id+"F0.wireOp",EDGE,"E1.top");var subQ8=sQuery(id+"F0.wireOp",EDGE,"E1.left");var subQ9=sQuery(id+"F0.wireOp",EDGE,"E1.right");var subQ10=sQuery(id+"F0.wireOp",EDGE,"E23.filletArc");var subQ11=sQuery(id+"F0.wireOp",EDGE,"E24.filletArc");Q0=makeQuery(id+"F2.boolean.opBoolean","SPLIT",FACE,{"disambiguationData":[TD([makeQuery(id+"F1.opExtrude","SWEPT_FACE",FACE,{"disambiguationData":[OSD([subQ5])]})])],"derivedFrom":makeQuery(id+"F1.opExtrude","CAP_FACE",FACE,{"disambiguationData":[OSD([subQ5,subQ7,subQ8,subQ9,subQ4,subQ3,subQ2,subQ1,subQ6,subQ0,subQ10,subQ11])],"isStart":true})});}
            var sketch = newSketch(context, id + "F16", { "sketchPlane" : qUnion([Q0])});
            skArc(sketch, "E79.0.0", {"start": v(14.05, 38.38) * mm, "mid": v(16.98, 31.31) * mm, "end": v(24.05, 28.38) * mm});
            skLineSegment(sketch, "E79.0.1", {"start": v(24.05, 28.38) * mm, "end": v(164.05, 28.38) * mm});
            skArc(sketch, "E79.0.2", {"start": v(164.05, 28.38) * mm, "mid": v(171.12, 31.31) * mm, "end": v(174.05, 38.38) * mm});
            skLineSegment(sketch, "E79.0.3", {"start": v(174.05, 38.38) * mm, "end": v(174.05, 198.38) * mm});
            skArc(sketch, "E79.0.4", {"start": v(174.05, 198.38) * mm, "mid": v(171.12, 205.45) * mm, "end": v(164.05, 208.38) * mm});
            skLineSegment(sketch, "E79.0.5", {"start": v(164.05, 208.38) * mm, "end": v(24.05, 208.38) * mm});
            skArc(sketch, "E79.0.6", {"start": v(24.05, 208.38) * mm, "mid": v(16.98, 205.45) * mm, "end": v(14.05, 198.38) * mm});
            skLineSegment(sketch, "E79.0.7", {"start": v(14.05, 198.38) * mm, "end": v(14.05, 38.38) * mm});
            skCircle(sketch, "E80.0", {"center": v(34.05, 50.88) * mm, "radius": 4 * mm});
            skCircle(sketch, "E81.0", {"center": v(34.05, 185.88) * mm, "radius": 4 * mm});
            skCircle(sketch, "E82.0", {"center": v(154.05, 185.88) * mm, "radius": 4 * mm});
            skLineSegment(sketch, "E83.0", {"start": v(154.05, 158.68) * mm, "end": v(154.05, 78.09) * mm});
            skArc(sketch, "E84.0", {"start": v(150.2, 70.2) * mm, "mid": v(153.04, 73.7) * mm, "end": v(154.05, 78.09) * mm});
            skArc(sketch, "E85.0", {"start": v(37.9, 70.2) * mm, "mid": v(94.05, 50.88) * mm, "end": v(150.2, 70.2) * mm});
            skArc(sketch, "E86.0", {"start": v(34.05, 78.09) * mm, "mid": v(35.06, 73.7) * mm, "end": v(37.9, 70.2) * mm});
            skLineSegment(sketch, "E87.0", {"start": v(34.05, 158.68) * mm, "end": v(34.05, 78.09) * mm});
            skArc(sketch, "E88.0", {"start": v(37.9, 166.56) * mm, "mid": v(35.06, 163.06) * mm, "end": v(34.05, 158.68) * mm});
            skArc(sketch, "E89.0", {"start": v(150.2, 166.56) * mm, "mid": v(94.05, 185.88) * mm, "end": v(37.9, 166.56) * mm});
            skArc(sketch, "E90.0", {"start": v(154.05, 158.68) * mm, "mid": v(153.04, 163.06) * mm, "end": v(150.2, 166.56) * mm});
            skLineSegment(sketch, "E91", {"start": v(94.05, 208.38) * mm, "end": v(94.05, 238.38) * mm, "construction": true});
            skCircle(sketch, "E92", {"center": v(94.05, 238.38) * mm, "radius": 6 * mm});
            skArc(sketch, "E93", {"start": v(79.05, 238.38) * mm, "mid": v(94.05, 253.38) * mm, "end": v(109.05, 238.38) * mm});
            skLineSegment(sketch, "E94", {"start": v(79.05, 238.38) * mm, "end": v(79.05, 226.38) * mm});
            skLineSegment(sketch, "E95", {"start": v(79.05, 226.38) * mm, "end": v(61.05, 208.38) * mm});
            skLineSegment(sketch, "E96.MirrorCS", {"start": v(109.05, 238.38) * mm, "end": v(109.05, 226.38) * mm});
            skLineSegment(sketch, "E97.MirrorCS", {"start": v(109.05, 226.38) * mm, "end": v(127.05, 208.38) * mm});
            skCircle(sketch, "E98.0", {"center": v(154.05, 50.88) * mm, "radius": 4 * mm});
            skLineSegment(sketch, "E99", {"start": v(14.05, 118.38) * mm, "end": v(174.05, 118.38) * mm, "construction": true});
            skLineSegment(sketch, "E100.MirrorCS", {"start": v(164.05, 28.38) * mm, "end": v(24.05, 28.38) * mm});
            skLineSegment(sketch, "E101.MirrorCS", {"start": v(109.05, -1.62) * mm, "end": v(109.05, 10.38) * mm});
            skLineSegment(sketch, "E102.MirrorCS", {"start": v(109.05, 10.38) * mm, "end": v(127.05, 28.38) * mm});
            skArc(sketch, "E103.MirrorCS", {"start": v(79.05, -1.62) * mm, "mid": v(94.05, -16.62) * mm, "end": v(109.05, -1.62) * mm});
            skCircle(sketch, "E104.MirrorC", {"center": v(94.05, -1.62) * mm, "radius": 6 * mm});
            skLineSegment(sketch, "E105.MirrorCS", {"start": v(79.05, -1.62) * mm, "end": v(79.05, 10.38) * mm});
            skLineSegment(sketch, "E106.MirrorCS", {"start": v(94.05, 28.38) * mm, "end": v(94.05, -1.62) * mm, "construction": true});
            skLineSegment(sketch, "E107.MirrorCS", {"start": v(79.05, 10.38) * mm, "end": v(61.05, 28.38) * mm});
            skSolve(sketch);
        }
        {
            var Q0;
            Q0=qSketchRegion(id+"F16",true);
            var Q1;
            Q1=makeQuery(id+"F2.opExtrude","CAP_FACE",FACE,{"disambiguationData":[OSD([sQuery(id+"F0.wireOp",EDGE,"E12"),sQuery(id+"F0.wireOp",EDGE,"E13"),sQuery(id+"F0.wireOp",EDGE,"E14"),sQuery(id+"F0.wireOp",EDGE,"E15"),sQuery(id+"F0.wireOp",EDGE,"E17.filletArc"),sQuery(id+"F0.wireOp",EDGE,"E18.filletArc"),sQuery(id+"F0.wireOp",EDGE,"E19.filletArc"),sQuery(id+"F0.wireOp",EDGE,"E20.filletArc"),sQuery(id+"F0.wireOp",EDGE,"E25.0"),sQuery(id+"F0.wireOp",EDGE,"E25.1"),sQuery(id+"F0.wireOp",EDGE,"E25.2"),sQuery(id+"F0.wireOp",EDGE,"E25.3"),sQuery(id+"F0.wireOp",EDGE,"E25.4"),sQuery(id+"F0.wireOp",EDGE,"E25.5"),sQuery(id+"F0.wireOp",EDGE,"E25.6"),sQuery(id+"F0.wireOp",EDGE,"E25.7")])],"isStart":false});
            extrude(context, id + "F17", {"entities" : qUnion([Q0]), "endBound" : BoundingType.UP_TO_SURFACE, "endBoundEntityFace" : qUnion([Q1]), "depth" : 25 * mm});
        }
    });
